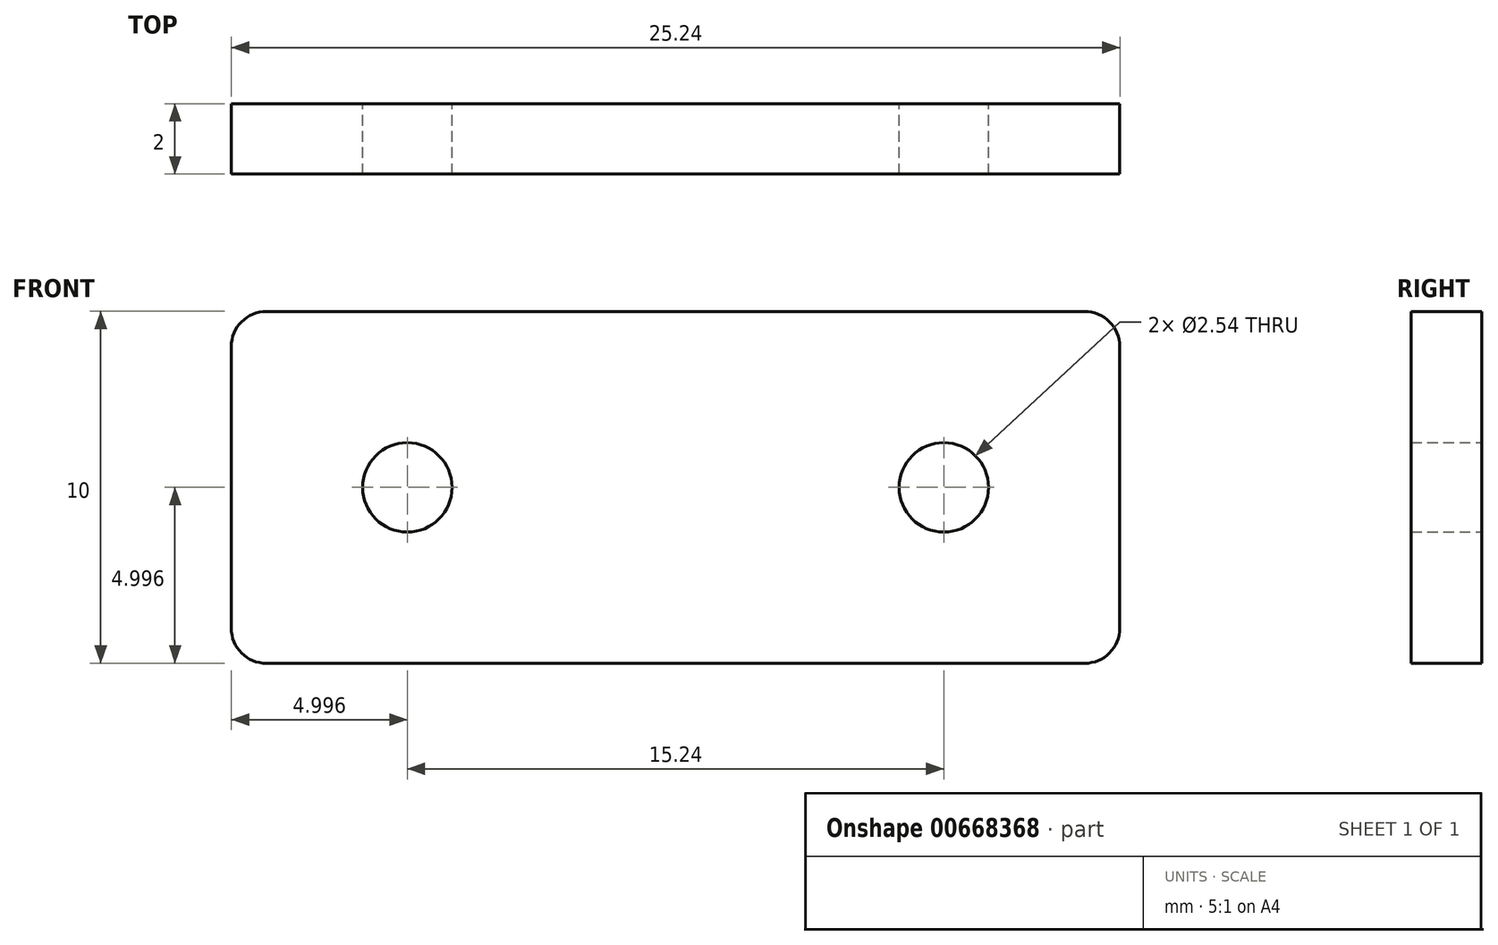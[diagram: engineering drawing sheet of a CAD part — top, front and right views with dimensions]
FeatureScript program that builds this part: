
annotation { "Feature Type Name" : "Feature", "Feature Type Description" : "" }
export const myFeature = defineFeature(function(context is Context, id is Id, definition is map)
    precondition{}
    {
        {
            var Q0;
            Q0=qCreatedBy(makeId("Front.planeOp"),FACE);
            var sketch = newSketch(context, id + "F0", { "sketchPlane" : qUnion([Q0])});
            skLineSegment(sketch, "E0.bottom", {"start": v(-18.96, 7.95) * mm, "end": v(4.28, 7.95) * mm});
            skLineSegment(sketch, "E0.top", {"start": v(-18.96, -2.05) * mm, "end": v(4.28, -2.05) * mm});
            skLineSegment(sketch, "E0.left", {"start": v(-19.96, 6.95) * mm, "end": v(-19.96, -1.05) * mm});
            skLineSegment(sketch, "E0.right", {"start": v(5.28, 6.95) * mm, "end": v(5.28, -1.05) * mm});
            skCircle(sketch, "E1", {"center": v(-14.96, 2.95) * mm, "radius": 1.27 * mm});
            skCircle(sketch, "E2", {"center": v(0.28, 2.95) * mm, "radius": 1.27 * mm});
            skPoint(sketch, "E3.visualSharp", {"position": v(-19.96, 7.95) * mm});
            skArc(sketch, "E3.filletArc", {"start": v(-18.96, 7.95) * mm, "mid": v(-19.67, 7.65) * mm, "end": v(-19.96, 6.95) * mm});
            skPoint(sketch, "E4.visualSharp", {"position": v(5.28, 7.95) * mm});
            skArc(sketch, "E4.filletArc", {"start": v(5.28, 6.95) * mm, "mid": v(4.98, 7.65) * mm, "end": v(4.28, 7.95) * mm});
            skPoint(sketch, "E5.visualSharp", {"position": v(5.28, -2.05) * mm});
            skArc(sketch, "E5.filletArc", {"start": v(4.28, -2.05) * mm, "mid": v(4.98, -1.76) * mm, "end": v(5.28, -1.05) * mm});
            skPoint(sketch, "E6.visualSharp", {"position": v(-19.96, -2.05) * mm});
            skArc(sketch, "E6.filletArc", {"start": v(-19.96, -1.05) * mm, "mid": v(-19.67, -1.76) * mm, "end": v(-18.96, -2.05) * mm});
            skSolve(sketch);
        }
        {
            var Q0;
            Q0=makeQuery(id+"F0.imprint","IMPRINT",FACE,{"disambiguationData":[TD([[makeQuery(id+"F0.imprint","IMPRINT",EDGE,{"derivedFrom":sQuery(id+"F0.wireOp",EDGE,"E0.bottom")}),-1.0]])]});
            extrude(context, id + "F1", {"entities" : qUnion([Q0]), "depth" : 2 * mm, "offsetDistance" : 25 * mm});
        }
    });
